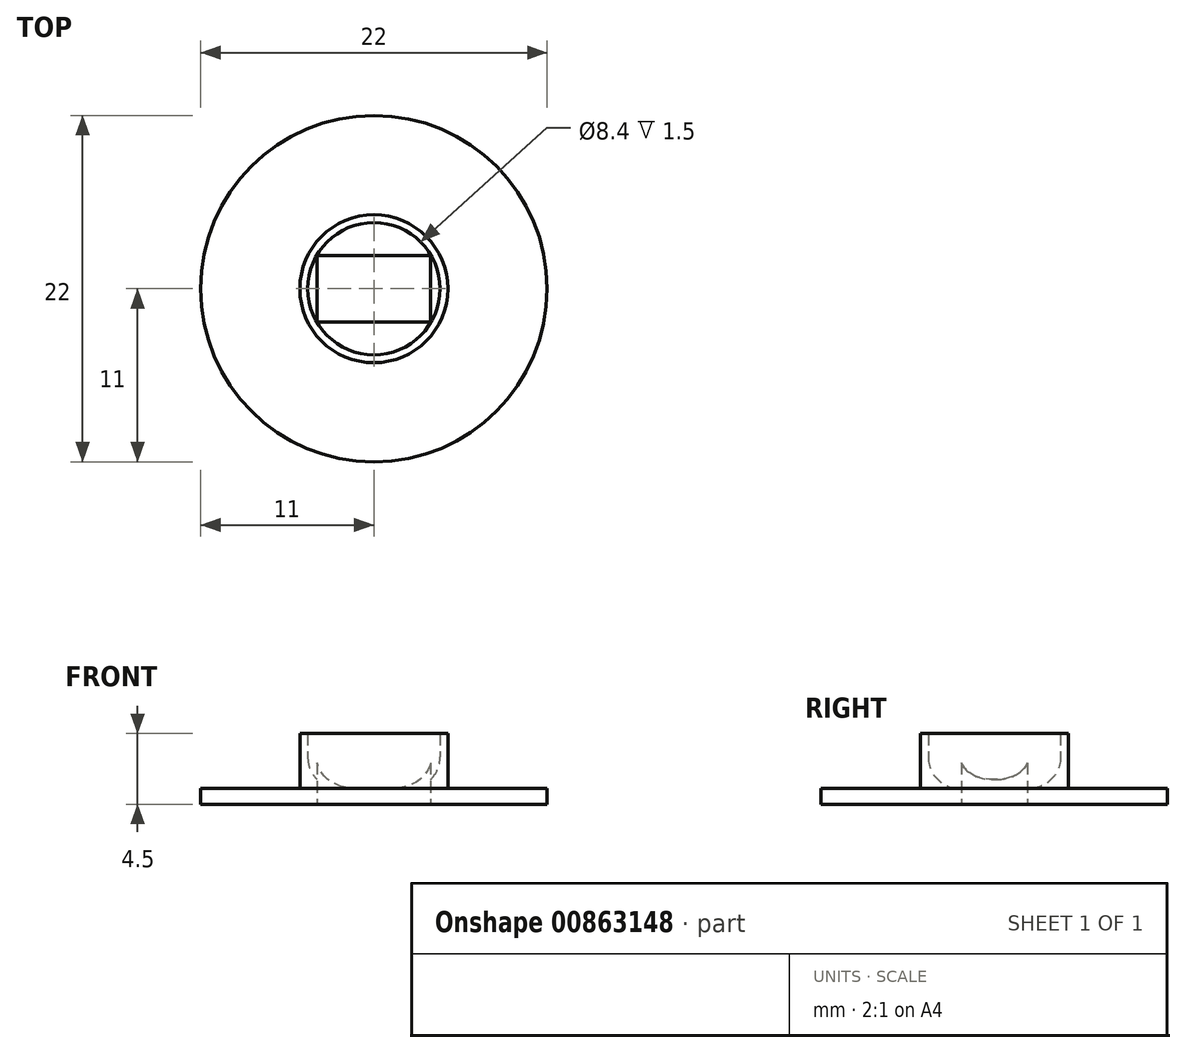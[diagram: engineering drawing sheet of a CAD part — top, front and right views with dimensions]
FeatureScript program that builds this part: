
annotation { "Feature Type Name" : "Feature", "Feature Type Description" : "" }
export const myFeature = defineFeature(function(context is Context, id is Id, definition is map)
    precondition{}
    {
        {
            var Q0;
            Q0=qCreatedBy(makeId("Top.planeOp"),FACE);
            var sketch = newSketch(context, id + "F0", { "sketchPlane" : qUnion([Q0])});
            skCircle(sketch, "E0", {"center": v(0, 0) * mm, "radius": 11 * mm});
            skLineSegment(sketch, "E1.bottom", {"start": v(-3.6, 2.1) * mm, "end": v(3.6, 2.1) * mm});
            skLineSegment(sketch, "E1.top", {"start": v(-3.6, -2.1) * mm, "end": v(3.6, -2.1) * mm});
            skLineSegment(sketch, "E1.left", {"start": v(-3.6, 2.1) * mm, "end": v(-3.6, -2.1) * mm});
            skLineSegment(sketch, "E1.right", {"start": v(3.6, 2.1) * mm, "end": v(3.6, -2.1) * mm});
            skSolve(sketch);
        }
        {
            var Q0;
            Q0=qSketchRegion(id+"F0",true);
            extrude(context, id + "F1", {"entities" : qUnion([Q0]), "depth" : 1 * mm, "offsetDistance" : 25 * mm});
        }
        {
            var Q0;
            Q0=makeQuery(id+"F1.opExtrude","CAP_FACE",FACE,{"disambiguationData":[OSD([sQuery(id+"F0.wireOp",EDGE,"E0"),sQuery(id+"F0.wireOp",EDGE,"czUkiF2n-v74J-udwk-3dqZ-0WtBXZ1AYgIj")])],"isStart":false});
            var sketch = newSketch(context, id + "F2", { "sketchPlane" : qUnion([Q0])});
            skCircle(sketch, "E2", {"center": v(0, 0) * mm, "radius": 4.2 * mm});
            skCircle(sketch, "E3", {"center": v(0, 0) * mm, "radius": 4.7 * mm});
            skSolve(sketch);
        }
        {
            var Q0;
            Q0=qSketchRegion(id+"F2",true);
            extrude(context, id + "F3", {"entities" : qUnion([Q0]), "operationType" : NewBodyOperationType.ADD, "depth" : 3.5 * mm, "offsetDistance" : 25 * mm});
        }
        {
            var Q0;
            Q0=makeQuery(id+"F3.opExtrude","CAP_EDGE",EDGE,{"disambiguationData":[OSD([sQuery(id+"F2.wireOp",EDGE,"E2")])],"isStart":true});
            fillet(context, id + "F4", {"entities" : qUnion([Q0]), "radius" : 2 * mm, "tangentPropagation" : true, "allowEdgeOverflow" : false});
        }
    });
